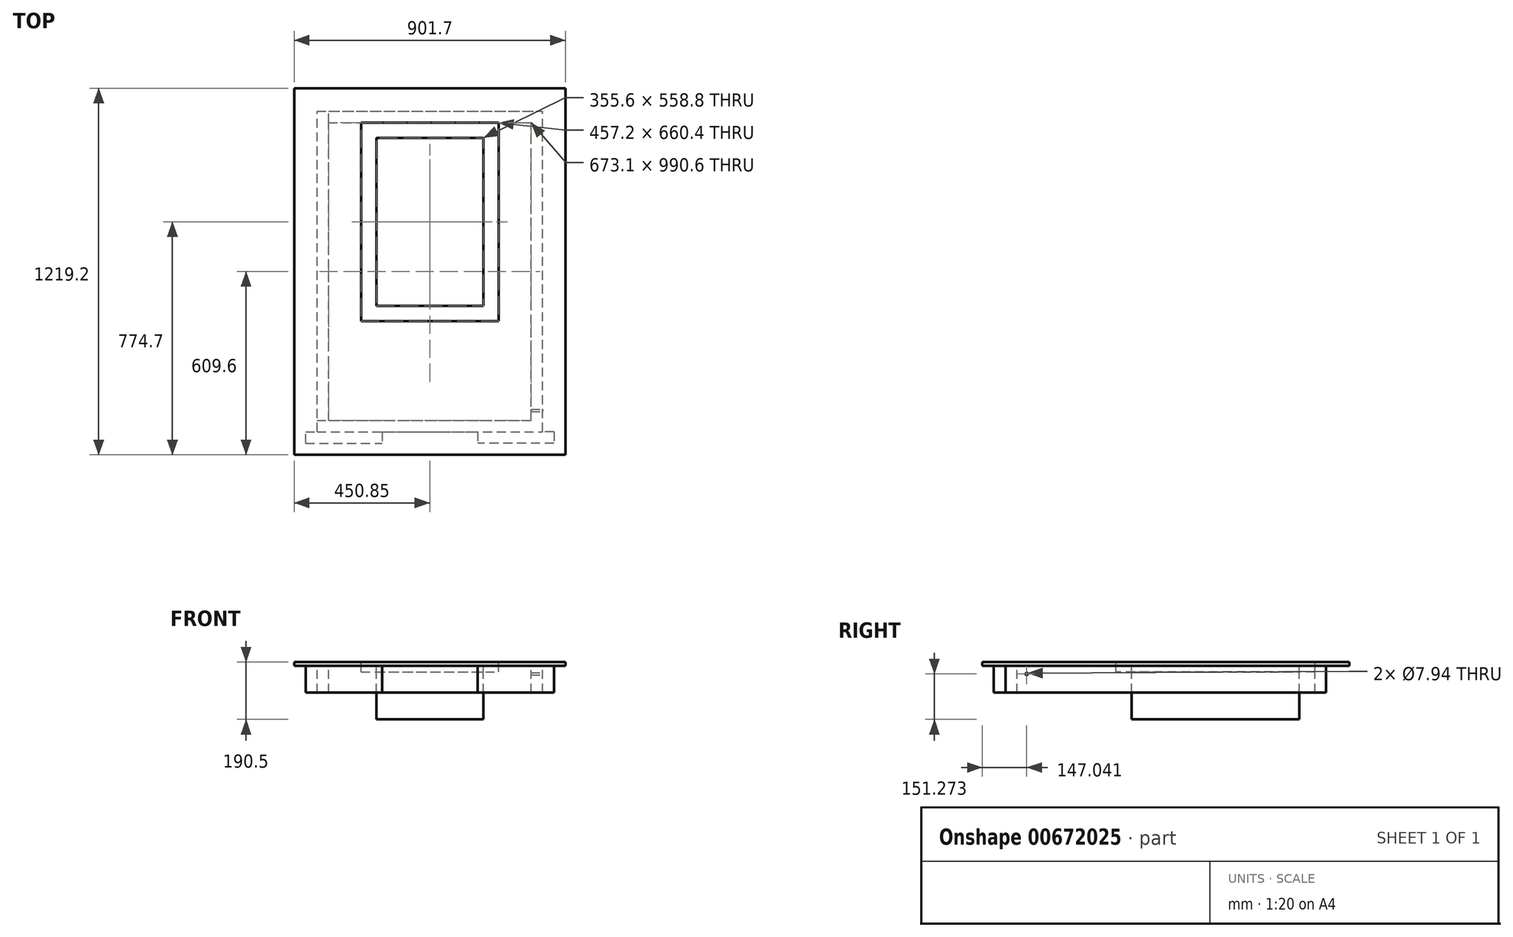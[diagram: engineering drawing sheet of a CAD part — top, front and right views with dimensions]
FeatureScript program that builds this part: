
annotation { "Feature Type Name" : "Feature", "Feature Type Description" : "" }
export const myFeature = defineFeature(function(context is Context, id is Id, definition is map)
    precondition{}
    {
        {
            var Q0;
            Q0=qCreatedBy(makeId("Top.planeOp"),FACE);
            var sketch = newSketch(context, id + "F0", { "sketchPlane" : qUnion([Q0])});
            skLineSegment(sketch, "E0.bottom", {"start": v(0, 0) * mm, "end": v(901.7, 0) * mm});
            skLineSegment(sketch, "E0.top", {"start": v(0, 1219.2) * mm, "end": v(901.7, 1219.2) * mm});
            skLineSegment(sketch, "E0.left", {"start": v(0, 0) * mm, "end": v(0, 1219.2) * mm});
            skLineSegment(sketch, "E0.right", {"start": v(901.7, 0) * mm, "end": v(901.7, 1219.2) * mm});
            skLineSegment(sketch, "E1.bottom", {"start": v(222.25, 1104.9) * mm, "end": v(679.45, 1104.9) * mm});
            skLineSegment(sketch, "E1.top", {"start": v(222.25, 444.5) * mm, "end": v(679.45, 444.5) * mm});
            skLineSegment(sketch, "E1.left", {"start": v(222.25, 1104.9) * mm, "end": v(222.25, 774.7) * mm});
            skLineSegment(sketch, "E1.right", {"start": v(679.45, 1104.9) * mm, "end": v(679.45, 444.5) * mm});
            skPoint(sketch, "E2", {"position": v(0, 774.7) * mm});
            skPoint(sketch, "E3", {"position": v(222.25, 774.7) * mm});
            skPoint(sketch, "E4", {"position": v(679.45, 774.7) * mm});
            skPoint(sketch, "E5", {"position": v(901.7, 774.7) * mm});
            skLineSegment(sketch, "E6", {"start": v(323.85, 774.7) * mm, "end": v(325.19, 774.7) * mm});
            skPoint(sketch, "E7", {"position": v(323.85, 774.7) * mm});
            skPoint(sketch, "E8", {"position": v(577.85, 774.7) * mm});
            skLineSegment(sketch, "E9", {"start": v(222.25, 774.7) * mm, "end": v(222.25, 444.5) * mm});
            skLineSegment(sketch, "E10", {"start": v(325.19, 774.7) * mm, "end": v(576.7, 774.7) * mm});
            skLineSegment(sketch, "E11", {"start": v(576.7, 774.7) * mm, "end": v(577.85, 774.7) * mm});
            skLineSegment(sketch, "E12.bottom", {"start": v(293.4, 742.86) * mm, "end": v(626.8, 742.86) * mm});
            skLineSegment(sketch, "E12.top", {"start": v(293.4, 811.01) * mm, "end": v(626.8, 811.01) * mm});
            skLineSegment(sketch, "E12.left", {"start": v(293.4, 742.86) * mm, "end": v(293.4, 811.01) * mm});
            skLineSegment(sketch, "E12.right", {"start": v(626.8, 742.86) * mm, "end": v(626.8, 811.01) * mm});
            skSolve(sketch);
        }
        {
            var Q0;
            Q0=makeQuery(id+"F0.imprint","IMPRINT",FACE,{"disambiguationData":[TD([[makeQuery(id+"F0.imprint","IMPRINT",EDGE,{"derivedFrom":sQuery(id+"F0.wireOp",EDGE,"E0.bottom")}),1.0]])]});
            extrude(context, id + "F1", {"entities" : qUnion([Q0]), "oppositeDirection" : true, "depth" : 12.7 * mm, "offsetDistance" : 25.4 * mm});
        }
        {
            var Q0;
            Q0=makeQuery(id+"F1.opExtrude","CAP_FACE",FACE,{"disambiguationData":[OSD([sQuery(id+"F0.wireOp",EDGE,"E0.bottom"),sQuery(id+"F0.wireOp",EDGE,"E0.top"),sQuery(id+"F0.wireOp",EDGE,"E0.left"),sQuery(id+"F0.wireOp",EDGE,"E0.right"),sQuery(id+"F0.wireOp",EDGE,"E1.bottom"),sQuery(id+"F0.wireOp",EDGE,"E1.top"),sQuery(id+"F0.wireOp",EDGE,"E1.left"),sQuery(id+"F0.wireOp",EDGE,"E1.right"),sQuery(id+"F0.wireOp",EDGE,"E9")])],"isStart":false});
            var sketch = newSketch(context, id + "F2", { "sketchPlane" : qUnion([Q0])});
            skLineSegment(sketch, "E13.bottom", {"start": v(0, -1143) * mm, "end": v(901.7, -1143) * mm});
            skLineSegment(sketch, "E13.top", {"start": v(0, -1104.9) * mm, "end": v(901.7, -1104.9) * mm});
            skLineSegment(sketch, "E13.left", {"start": v(0, -1143) * mm, "end": v(0, -1104.9) * mm});
            skLineSegment(sketch, "E13.right", {"start": v(901.7, -1143) * mm, "end": v(901.7, -1104.9) * mm});
            skLineSegment(sketch, "E14", {"start": v(146.05, -1104.9) * mm, "end": v(146.05, -444.5) * mm});
            skLineSegment(sketch, "E15", {"start": v(146.05, -444.5) * mm, "end": v(146.05, -368.3) * mm});
            skLineSegment(sketch, "E16", {"start": v(146.05, -368.3) * mm, "end": v(755.65, -368.3) * mm});
            skLineSegment(sketch, "E17", {"start": v(755.65, -368.3) * mm, "end": v(755.65, -1104.9) * mm});
            skLineSegment(sketch, "E18", {"start": v(273.05, -1054.1) * mm, "end": v(628.65, -1054.1) * mm});
            skLineSegment(sketch, "E19", {"start": v(628.65, -1054.1) * mm, "end": v(628.65, -495.3) * mm});
            skLineSegment(sketch, "E20", {"start": v(628.65, -495.3) * mm, "end": v(273.05, -495.3) * mm});
            skLineSegment(sketch, "E21", {"start": v(273.05, -495.3) * mm, "end": v(273.05, -1054.1) * mm});
            skSolve(sketch);
        }
        {
            var Q0;
            Q0=makeQuery(id+"F2.imprint","IMPRINT",FACE,{"disambiguationData":[TD([[makeQuery(id+"F2.imprint","IMPRINT",EDGE,{"derivedFrom":sQuery(id+"F2.wireOp",EDGE,"E18")}),1.0]])]});
            extrude(context, id + "F3", {"entities" : qUnion([Q0]), "depth" : 177.8 * mm, "offsetDistance" : 25.4 * mm});
        }
        {
            var Q0;
            Q0=makeQuery(id+"F2.imprint","IMPRINT",FACE,{"disambiguationData":[TD([[makeQuery(id+"F2.imprint","IMPRINT",EDGE,{"derivedFrom":sQuery(id+"F2.wireOp",EDGE,"E18")}),-1.0]])]});
            extrude(context, id + "F4", {"entities" : qUnion([Q0]), "depth" : 19.26 * mm, "offsetDistance" : 25.4 * mm});
        }
        {
            var Q0;
            Q0=makeQuery(id+"F1.opExtrude","CAP_FACE",FACE,{"disambiguationData":[OSD([sQuery(id+"F0.wireOp",EDGE,"E0.bottom"),sQuery(id+"F0.wireOp",EDGE,"E0.top"),sQuery(id+"F0.wireOp",EDGE,"E0.left"),sQuery(id+"F0.wireOp",EDGE,"E0.right"),sQuery(id+"F0.wireOp",EDGE,"E1.bottom"),sQuery(id+"F0.wireOp",EDGE,"E1.top"),sQuery(id+"F0.wireOp",EDGE,"E1.left"),sQuery(id+"F0.wireOp",EDGE,"E1.right"),sQuery(id+"F0.wireOp",EDGE,"E9")])],"isStart":false});
            var sketch = newSketch(context, id + "F5", { "sketchPlane" : qUnion([Q0])});
            skLineSegment(sketch, "E22.bottom", {"start": v(76.2, -76.2) * mm, "end": v(787.4, -76.2) * mm});
            skLineSegment(sketch, "E22.top", {"start": v(76.2, -114.3) * mm, "end": v(787.4, -114.3) * mm});
            skLineSegment(sketch, "E22.left", {"start": v(76.2, -76.2) * mm, "end": v(76.2, -114.3) * mm});
            skLineSegment(sketch, "E22.right", {"start": v(787.4, -76.2) * mm, "end": v(787.4, -114.3) * mm});
            skLineSegment(sketch, "E23.bottom", {"start": v(76.2, -114.3) * mm, "end": v(114.3, -114.3) * mm});
            skLineSegment(sketch, "E23.top", {"start": v(114.3, -1143) * mm, "end": v(114.3, -1143) * mm});
            skLineSegment(sketch, "E23.left", {"start": v(76.2, -114.3) * mm, "end": v(76.2, -1143) * mm});
            skLineSegment(sketch, "E23.right", {"start": v(114.3, -114.3) * mm, "end": v(114.3, -1143) * mm});
            skLineSegment(sketch, "E24.bottom", {"start": v(787.4, -76.2) * mm, "end": v(825.5, -76.2) * mm});
            skLineSegment(sketch, "E24.left", {"start": v(787.4, -76.2) * mm, "end": v(787.4, -1104.9) * mm});
            skLineSegment(sketch, "E24.right", {"start": v(825.5, -76.2) * mm, "end": v(825.5, -1143) * mm});
            skLineSegment(sketch, "E25", {"start": v(76.2, -1143) * mm, "end": v(114.3, -1143) * mm});
            skPoint(sketch, "E26", {"position": v(114.3, -1104.9) * mm});
            skLineSegment(sketch, "E27", {"start": v(114.3, -1104.9) * mm, "end": v(787.4, -1104.9) * mm});
            skLineSegment(sketch, "E28", {"start": v(114.3, -1143) * mm, "end": v(825.5, -1143) * mm});
            skLineSegment(sketch, "E29", {"start": v(787.4, -1104.9) * mm, "end": v(825.5, -1104.9) * mm});
            skLineSegment(sketch, "E30.bottom", {"start": v(863.6, -76.2) * mm, "end": v(609.6, -76.2) * mm});
            skLineSegment(sketch, "E30.top", {"start": v(863.6, -38.1) * mm, "end": v(609.6, -38.1) * mm});
            skLineSegment(sketch, "E30.left", {"start": v(863.6, -76.2) * mm, "end": v(863.6, -38.1) * mm});
            skLineSegment(sketch, "E30.right", {"start": v(609.6, -76.2) * mm, "end": v(609.6, -38.1) * mm});
            skLineSegment(sketch, "E31.MirrorCS", {"start": v(292.1, -76.2) * mm, "end": v(292.1, -38.1) * mm});
            skLineSegment(sketch, "E32.MirrorCS", {"start": v(38.1, -38.1) * mm, "end": v(292.1, -38.1) * mm});
            skLineSegment(sketch, "E33", {"start": v(863.6, -76.2) * mm, "end": v(825.5, -76.2) * mm});
            skLineSegment(sketch, "E34", {"start": v(38.1, -76.2) * mm, "end": v(76.2, -76.2) * mm});
            skPoint(sketch, "E35.start.orphan", {"position": v(450.85, 0) * mm});
            skLineSegment(sketch, "E36", {"start": v(38.1, -38.1) * mm, "end": v(38.1, -76.2) * mm});
            skSolve(sketch);
        }
        {
            var Q0;
            {var subQ1=sQuery(id+"F5.wireOp",EDGE,"E22.bottom");Q0=makeQuery(id+"F5.imprint","IMPRINT",FACE,{"disambiguationData":[TD([[makeQuery(id+"F5.imprint","IMPRINT",EDGE,{"derivedFrom":subQ1}),-1.0]])]});}
            var Q1;
            {var subQ3=sQuery(id+"F5.wireOp",EDGE,"E23.bottom");Q1=makeQuery(id+"F5.imprint","IMPRINT",FACE,{"disambiguationData":[TD([[makeQuery(id+"F5.imprint","IMPRINT",EDGE,{"derivedFrom":subQ3}),-1.0]])]});}
            var Q2;
            {var subQ5=sQuery(id+"F5.wireOp",EDGE,"E28");Q2=makeQuery(id+"F5.imprint","IMPRINT",FACE,{"disambiguationData":[TD([[makeQuery(id+"F5.imprint","IMPRINT",EDGE,{"derivedFrom":subQ5}),1.0]])]});}
            var Q3;
            {var subQ1=sQuery(id+"F5.wireOp",EDGE,"E24.bottom");Q3=makeQuery(id+"F5.imprint","IMPRINT",FACE,{"disambiguationData":[TD([[makeQuery(id+"F5.imprint","IMPRINT",EDGE,{"derivedFrom":subQ1}),-1.0]])]});}
            extrude(context, id + "F6", {"entities" : qUnion([Q0, Q1, Q2, Q3]), "depth" : 88.9 * mm, "offsetDistance" : 25.4 * mm});
        }
        {
            var Q0;
            Q0 = qSketchRegion(id + "F5", true);
            extrude(context, id + "F7", {"entities" : qUnion([Q0]), "depth" : 88.9 * mm, "offsetDistance" : 25.4 * mm});
        }
        {
            var Q0;
            Q0=makeQuery(id+"F7.opExtrude","SWEPT_FACE",FACE,{"disambiguationData":[OSD([sQuery(id+"F5.wireOp",EDGE,"E24.right")])]});
            var sketch = newSketch(context, id + "F8", { "sketchPlane" : qUnion([Q0])});
            skLineSegment(sketch, "E37.0", {"start": v(76.2, -101.6) * mm, "end": v(76.2, -12.7) * mm});
            skLineSegment(sketch, "E38.0", {"start": v(76.2, -101.6) * mm, "end": v(1143, -101.6) * mm});
            skPoint(sketch, "E39", {"position": v(147.04, -39.23) * mm});
            skSolve(sketch);
        }
        {
            var Q0;
            Q0=makeQuery(id+"F8.imprint","IMPRINT",FACE,{"disambiguationData":[TD([[makeQuery(id+"F8.imprint","IMPRINT",EDGE,{"derivedFrom":sQuery(id+"F8.wireOp",EDGE,"E37.0")}),-1.0]])]});
            var sketch = newSketch(context, id + "F9", { "sketchPlane" : qUnion([Q0])});
            skPoint(sketch, "E40.0", {"position": v(147.04, -39.23) * mm});
            skCircle(sketch, "E41", {"center": v(147.04, -39.23) * mm, "radius": 3.97 * mm});
            skSolve(sketch);
        }
        {
            var Q0;
            Q0=makeQuery(id+"F9.imprint","IMPRINT",FACE,{"disambiguationData":[TD([[makeQuery(id+"F9.imprint","IMPRINT",EDGE,{"derivedFrom":sQuery(id+"F9.wireOp",EDGE,"E41")}),1.0]])]});
            extrude(context, id + "F10", {"entities" : qUnion([Q0]), "operationType" : NewBodyOperationType.REMOVE, "oppositeDirection" : true, "depth" : 63.5 * mm, "offsetDistance" : 25.4 * mm});
        }
    });
